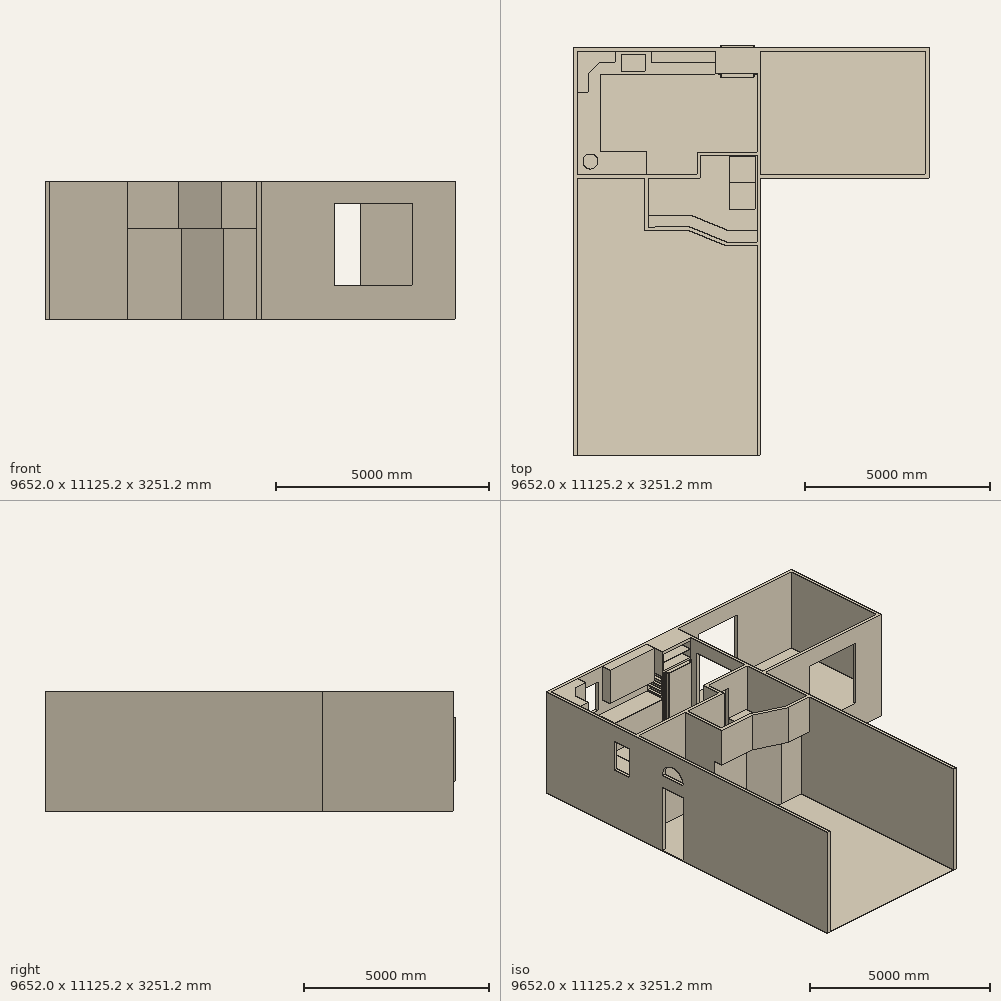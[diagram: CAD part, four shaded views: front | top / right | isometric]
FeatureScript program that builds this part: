
annotation { "Feature Type Name" : "Feature", "Feature Type Description" : "" }
export const myFeature = defineFeature(function(context is Context, id is Id, definition is map)
    precondition{}
    {
        {
            var Q0;
            Q0=qCreatedBy(makeId("Top.planeOp"),FACE);
            var sketch = newSketch(context, id + "F0", { "sketchPlane" : qUnion([Q0])});
            skLineSegment(sketch, "E0.bottom", {"start": v(-4876.8, 3352.8) * mm, "end": v(4572, 3352.8) * mm});
            skLineSegment(sketch, "E0.top", {"start": v(0, 0) * mm, "end": v(4572, 0) * mm});
            skLineSegment(sketch, "E0.left", {"start": v(-4876.8, 3352.8) * mm, "end": v(-4876.8, 0) * mm});
            skLineSegment(sketch, "E0.right", {"start": v(4572, 3352.8) * mm, "end": v(4572, 0) * mm});
            skLineSegment(sketch, "E1.left", {"start": v(-4876.8, 0) * mm, "end": v(-4876.8, -7620) * mm});
            skLineSegment(sketch, "E1.right", {"start": v(0, 0) * mm, "end": v(0, -7620) * mm});
            skLineSegment(sketch, "E2.0", {"start": v(101.6, -101.6) * mm, "end": v(101.6, -7620) * mm});
            skLineSegment(sketch, "E2.1", {"start": v(101.6, -101.6) * mm, "end": v(4673.6, -101.6) * mm});
            skLineSegment(sketch, "E2.2", {"start": v(-4978.4, 0) * mm, "end": v(-4978.4, -7620) * mm});
            skLineSegment(sketch, "E2.3", {"start": v(-4978.4, 3454.4) * mm, "end": v(-4978.4, 0) * mm});
            skLineSegment(sketch, "E2.4", {"start": v(-4978.4, 3454.4) * mm, "end": v(4673.6, 3454.4) * mm});
            skLineSegment(sketch, "E2.5", {"start": v(4673.6, 3454.4) * mm, "end": v(4673.6, -101.6) * mm});
            skLineSegment(sketch, "E3", {"start": v(-4978.4, -7620) * mm, "end": v(-4876.8, -7620) * mm});
            skLineSegment(sketch, "E4", {"start": v(0, -7620) * mm, "end": v(101.6, -7620) * mm});
            skSolve(sketch);
        }
        {
            var Q0;
            Q0=qSketchRegion(id+"F0",true);
            extrude(context, id + "F1", {"entities" : qUnion([Q0]), "depth" : 3251.2 * mm});
        }
        {
            var Q0;
            Q0=qCreatedBy(makeId("Top.planeOp"),FACE);
            var sketch = newSketch(context, id + "F2", { "sketchPlane" : qUnion([Q0])});
            skLineSegment(sketch, "E5.0", {"start": v(-4876.8, 3352.8) * mm, "end": v(-4876.8, -7620) * mm});
            skLineSegment(sketch, "E6.0", {"start": v(-4876.8, 3352.8) * mm, "end": v(4572, 3352.8) * mm});
            skLineSegment(sketch, "E7.0", {"start": v(4572, 3352.8) * mm, "end": v(4572, 0) * mm});
            skLineSegment(sketch, "E8.0", {"start": v(0, 0) * mm, "end": v(4572, 0) * mm});
            skLineSegment(sketch, "E9.0", {"start": v(0, 0) * mm, "end": v(0, -7620) * mm});
            skLineSegment(sketch, "E10", {"start": v(-4876.8, -7620) * mm, "end": v(0, -7620) * mm});
            skSolve(sketch);
        }
        {
            var Q0;
            Q0=qSketchRegion(id+"F2",true);
            extrude(context, id + "F3", {"entities" : qUnion([Q0]), "operationType" : NewBodyOperationType.ADD, "depth" : 812.8 * mm});
        }
        {
            var Q0;
            Q0=makeQuery(id+"F3.opExtrude","CAP_FACE",FACE,{"disambiguationData":[OSD([sQuery(id+"F2.wireOp",EDGE,"E5.0"),sQuery(id+"F2.wireOp",EDGE,"E6.0"),sQuery(id+"F2.wireOp",EDGE,"E7.0"),sQuery(id+"F2.wireOp",EDGE,"E8.0"),sQuery(id+"F2.wireOp",EDGE,"E9.0"),sQuery(id+"F2.wireOp",EDGE,"E10")])],"isStart":false});
            var sketch = newSketch(context, id + "F4", { "sketchPlane" : qUnion([Q0])});
            skLineSegment(sketch, "E11", {"start": v(-4876.8, 0) * mm, "end": v(-3048, 0) * mm});
            skLineSegment(sketch, "E12", {"start": v(-3048, -1219.2) * mm, "end": v(-1778, -1219.2) * mm});
            skLineSegment(sketch, "E13", {"start": v(0, -1625.6) * mm, "end": v(0, -7620) * mm});
            skLineSegment(sketch, "E14", {"start": v(0, -7620) * mm, "end": v(-4876.8, -7620) * mm});
            skLineSegment(sketch, "E15", {"start": v(-4876.8, -7620) * mm, "end": v(-4876.8, 0) * mm});
            skLineSegment(sketch, "E16", {"start": v(-3048, 0) * mm, "end": v(-3048, -1219.2) * mm});
            skLineSegment(sketch, "E17", {"start": v(-1778, -1219.2) * mm, "end": v(-781.81, -1625.6) * mm});
            skLineSegment(sketch, "E18", {"start": v(-781.81, -1625.6) * mm, "end": v(0, -1625.6) * mm});
            skSolve(sketch);
        }
        {
            var Q0;
            Q0=qSketchRegion(id+"F4",true);
            extrude(context, id + "F5", {"entities" : qUnion([Q0]), "operationType" : NewBodyOperationType.REMOVE, "oppositeDirection" : true, "depth" : 800.1 * mm});
        }
        {
            var Q0;
            Q0=makeQuery(id+"F1.opExtrude","CAP_FACE",FACE,{"disambiguationData":[OSD([sQuery(id+"F0.wireOp",EDGE,"E0.bottom"),sQuery(id+"F0.wireOp",EDGE,"E0.top"),sQuery(id+"F0.wireOp",EDGE,"E0.left"),sQuery(id+"F0.wireOp",EDGE,"E0.right"),sQuery(id+"F0.wireOp",EDGE,"E1.left"),sQuery(id+"F0.wireOp",EDGE,"E1.right"),sQuery(id+"F0.wireOp",EDGE,"E2.0"),sQuery(id+"F0.wireOp",EDGE,"E2.1"),sQuery(id+"F0.wireOp",EDGE,"E2.2"),sQuery(id+"F0.wireOp",EDGE,"E2.3"),sQuery(id+"F0.wireOp",EDGE,"E2.4"),sQuery(id+"F0.wireOp",EDGE,"E2.5"),sQuery(id+"F0.wireOp",EDGE,"E3"),sQuery(id+"F0.wireOp",EDGE,"E4")])],"isStart":false});
            var sketch = newSketch(context, id + "F6", { "sketchPlane" : qUnion([Q0])});
            skLineSegment(sketch, "E19", {"start": v(-1625.6, 0) * mm, "end": v(-4876.8, 0) * mm});
            skLineSegment(sketch, "E20", {"start": v(-4876.8, 0) * mm, "end": v(-4876.8, -101.6) * mm});
            skLineSegment(sketch, "E21", {"start": v(-4876.8, -101.6) * mm, "end": v(-3048, -101.6) * mm});
            skLineSegment(sketch, "E22", {"start": v(-781.93, -1625.6) * mm, "end": v(-1778, -1219.2) * mm});
            skLineSegment(sketch, "E23", {"start": v(-1758.07, -1117.6) * mm, "end": v(-762, -1524) * mm});
            skLineSegment(sketch, "E24", {"start": v(-1778, -1219.2) * mm, "end": v(-3048, -1219.2) * mm});
            skLineSegment(sketch, "E25", {"start": v(-2946.4, -1117.6) * mm, "end": v(-1758.07, -1117.6) * mm});
            skPoint(sketch, "E26.orphan", {"position": v(-1778, -1117.6) * mm});
            skLineSegment(sketch, "E27", {"start": v(-3048, -1219.2) * mm, "end": v(-3048, -101.6) * mm});
            skLineSegment(sketch, "E28", {"start": v(-2946.4, -1117.6) * mm, "end": v(-2946.4, -101.6) * mm});
            skLineSegment(sketch, "E29.trimOffspring", {"start": v(-2946.4, -101.6) * mm, "end": v(-1524, -101.6) * mm});
            skLineSegment(sketch, "E30", {"start": v(-762, -1524) * mm, "end": v(0, -1524) * mm});
            skLineSegment(sketch, "E31", {"start": v(0, -1524) * mm, "end": v(0, -1625.6) * mm});
            skLineSegment(sketch, "E32", {"start": v(0, -1625.6) * mm, "end": v(-781.93, -1625.6) * mm});
            skLineSegment(sketch, "E33", {"start": v(0, 508) * mm, "end": v(-1524, 508) * mm});
            skLineSegment(sketch, "E34", {"start": v(-1524, 508) * mm, "end": v(-1524, -101.6) * mm});
            skLineSegment(sketch, "E35", {"start": v(0, 609.6) * mm, "end": v(-1625.6, 609.6) * mm});
            skLineSegment(sketch, "E36", {"start": v(-1625.6, 609.6) * mm, "end": v(-1625.6, 0) * mm});
            skLineSegment(sketch, "E37", {"start": v(0, 609.6) * mm, "end": v(0, 508) * mm});
            skSolve(sketch);
        }
        {
            var Q0;
            Q0=qSketchRegion(id+"F6",true);
            extrude(context, id + "F7", {"entities" : qUnion([Q0]), "endBound" : BoundingType.UP_TO_NEXT, "oppositeDirection" : true, "depth" : 25.4 * mm});
        }
        {
            var Q0;
            Q0=makeQuery(id+"F1.opExtrude","SWEPT_FACE",FACE,{"disambiguationData":[OSD([sQuery(id+"F0.wireOp",EDGE,"E2.2"),sQuery(id+"F0.wireOp",EDGE,"E2.3")])]});
            var sketch = newSketch(context, id + "F8", { "sketchPlane" : qUnion([Q0])});
            skLineSegment(sketch, "E38.bottom", {"start": v(1930.4, 12.7) * mm, "end": v(1117.6, 12.7) * mm});
            skLineSegment(sketch, "E38.top", {"start": v(1930.4, 2044.7) * mm, "end": v(1117.6, 2044.7) * mm});
            skLineSegment(sketch, "E38.left", {"start": v(1930.4, 12.7) * mm, "end": v(1930.4, 2044.7) * mm});
            skLineSegment(sketch, "E38.right", {"start": v(1117.6, 12.7) * mm, "end": v(1117.6, 2044.7) * mm});
            skLineSegment(sketch, "E39", {"start": v(1117.6, 2425.7) * mm, "end": v(1930.4, 2425.7) * mm});
            skArc(sketch, "E40", {"start": v(1930.4, 2425.7) * mm, "mid": v(1524, 2832.1) * mm, "end": v(1117.6, 2425.7) * mm});
            skSolve(sketch);
        }
        {
            var Q0;
            Q0=qSketchRegion(id+"F8",true);
            extrude(context, id + "F9", {"entities" : qUnion([Q0]), "operationType" : NewBodyOperationType.REMOVE, "oppositeDirection" : true, "depth" : 101.6 * mm});
        }
        {
            var Q0;
            Q0=makeQuery(id+"F1.opExtrude","SWEPT_FACE",FACE,{"disambiguationData":[OSD([sQuery(id+"F0.wireOp",EDGE,"E2.2"),sQuery(id+"F0.wireOp",EDGE,"E2.3")])]});
            var sketch = newSketch(context, id + "F10", { "sketchPlane" : qUnion([Q0])});
            skLineSegment(sketch, "E41.bottom", {"start": v(-787.4, 2743.2) * mm, "end": v(-177.8, 2743.2) * mm});
            skLineSegment(sketch, "E41.top", {"start": v(-787.4, 1828.8) * mm, "end": v(-177.8, 1828.8) * mm});
            skLineSegment(sketch, "E41.left", {"start": v(-787.4, 2743.2) * mm, "end": v(-787.4, 1828.8) * mm});
            skLineSegment(sketch, "E41.right", {"start": v(-177.8, 2743.2) * mm, "end": v(-177.8, 1828.8) * mm});
            skSolve(sketch);
        }
        {
            var Q0;
            Q0=qSketchRegion(id+"F10",true);
            extrude(context, id + "F11", {"entities" : qUnion([Q0]), "operationType" : NewBodyOperationType.REMOVE, "oppositeDirection" : true, "depth" : 101.6 * mm});
        }
        {
            var Q0;
            Q0=makeQuery(id+"FPiMINyQIs0wdXI_2.boolean.opBoolean","SPLIT",FACE,{"disambiguationData":[TD([makeQuery(id+"F1.opExtrude","SWEPT_FACE",FACE,{"disambiguationData":[OSD([sQuery(id+"F0.wireOp",EDGE,"E0.bottom")])]})])],"derivedFrom":makeQuery(id+"F3.opExtrude","CAP_FACE",FACE,{"disambiguationData":[OSD([sQuery(id+"F2.wireOp",EDGE,"E5.0"),sQuery(id+"F2.wireOp",EDGE,"E6.0"),sQuery(id+"F2.wireOp",EDGE,"E7.0"),sQuery(id+"F2.wireOp",EDGE,"E8.0"),sQuery(id+"F2.wireOp",EDGE,"E9.0"),sQuery(id+"F2.wireOp",EDGE,"E10")])],"isStart":false})});
            var sketch = newSketch(context, id + "F12", { "sketchPlane" : qUnion([Q0])});
            skLineSegment(sketch, "E42.top", {"start": v(-4876.8, 3352.8) * mm, "end": v(-4292.6, 3352.8) * mm});
            skLineSegment(sketch, "E42.left", {"start": v(-4876.8, 0) * mm, "end": v(-4876.8, 3352.8) * mm});
            skLineSegment(sketch, "E43.bottom", {"start": v(-4292.6, 3352.8) * mm, "end": v(-1117.6, 3352.8) * mm});
            skLineSegment(sketch, "E43.top", {"start": v(-4267.2, 2743.2) * mm, "end": v(-1117.6, 2743.2) * mm});
            skLineSegment(sketch, "E43.right", {"start": v(-1117.6, 3352.8) * mm, "end": v(-1117.6, 2743.2) * mm});
            skLineSegment(sketch, "E44", {"start": v(-4267.2, 2743.2) * mm, "end": v(-4267.2, 609.6) * mm});
            skLineSegment(sketch, "E45", {"start": v(-4267.2, 609.6) * mm, "end": v(-2997.2, 609.6) * mm});
            skLineSegment(sketch, "E46", {"start": v(-2997.2, 609.6) * mm, "end": v(-2997.2, 0) * mm});
            skLineSegment(sketch, "E47", {"start": v(-2997.2, 0) * mm, "end": v(-4876.8, 0) * mm});
            skSolve(sketch);
        }
        {
            var Q0;
            Q0=qSketchRegion(id+"F12",true);
            extrude(context, id + "F13", {"entities" : qUnion([Q0]), "depth" : 914.4 * mm});
        }
        {
            var Q0;
            Q0=makeQuery(id+"F13.opExtrude","CAP_FACE",FACE,{"disambiguationData":[OSD([sQuery(id+"F12.wireOp",EDGE,"E42.bottom"),sQuery(id+"F12.wireOp",EDGE,"E42.top"),sQuery(id+"F12.wireOp",EDGE,"E42.left"),sQuery(id+"F12.wireOp",EDGE,"E42.right"),sQuery(id+"F12.wireOp",EDGE,"E43.bottom"),sQuery(id+"F12.wireOp",EDGE,"E43.top"),sQuery(id+"F12.wireOp",EDGE,"E43.right")])],"isStart":false});
            var sketch = newSketch(context, id + "F14", { "sketchPlane" : qUnion([Q0])});
            skLineSegment(sketch, "E48", {"start": v(-1117.6, 3352.8) * mm, "end": v(-1117.6, 2717.8) * mm});
            skLineSegment(sketch, "E49", {"start": v(-1117.6, 2717.8) * mm, "end": v(-4241.8, 2717.8) * mm});
            skLineSegment(sketch, "E50", {"start": v(-4241.8, 2717.8) * mm, "end": v(-4241.8, 635) * mm});
            skLineSegment(sketch, "E51", {"start": v(-4241.8, 635) * mm, "end": v(-2997.2, 635) * mm});
            skLineSegment(sketch, "E52", {"start": v(-2997.2, 635) * mm, "end": v(-2997.2, 0) * mm});
            skLineSegment(sketch, "E53", {"start": v(-2997.2, 0) * mm, "end": v(-4876.8, 0) * mm});
            skLineSegment(sketch, "E54", {"start": v(-4876.8, 0) * mm, "end": v(-4876.8, 3352.8) * mm});
            skLineSegment(sketch, "E55", {"start": v(-4876.8, 3352.8) * mm, "end": v(-1117.6, 3352.8) * mm});
            skSolve(sketch);
        }
        {
            var Q0;
            Q0=qSketchRegion(id+"F14",true);
            extrude(context, id + "F15", {"entities" : qUnion([Q0]), "depth" : 19.05 * mm});
        }
        {
            var Q0;
            Q0=makeQuery(id+"F1.opExtrude","SWEPT_FACE",FACE,{"disambiguationData":[OSD([sQuery(id+"F0.wireOp",EDGE,"E2.1")])]});
            var sketch = newSketch(context, id + "F16", { "sketchPlane" : qUnion([Q0])});
            skLineSegment(sketch, "E56.bottom", {"start": v(1828.8, 2743.2) * mm, "end": v(3657.6, 2743.2) * mm});
            skLineSegment(sketch, "E56.top", {"start": v(1828.8, 812.8) * mm, "end": v(3657.6, 812.8) * mm});
            skLineSegment(sketch, "E56.left", {"start": v(1828.8, 2743.2) * mm, "end": v(1828.8, 812.8) * mm});
            skLineSegment(sketch, "E56.right", {"start": v(3657.6, 2743.2) * mm, "end": v(3657.6, 812.8) * mm});
            skSolve(sketch);
        }
        {
            var Q0;
            Q0=qSketchRegion(id+"F16",true);
            extrude(context, id + "F17", {"entities" : qUnion([Q0]), "operationType" : NewBodyOperationType.REMOVE, "oppositeDirection" : true, "depth" : 101.6 * mm});
        }
        {
            var Q0;
            Q0=makeQuery(id+"F1.opExtrude","SWEPT_FACE",FACE,{"disambiguationData":[OSD([sQuery(id+"F0.wireOp",EDGE,"E2.4")])]});
            var sketch = newSketch(context, id + "F18", { "sketchPlane" : qUnion([Q0])});
            skLineSegment(sketch, "E57.bottom", {"start": v(-2438.4, 2743.2) * mm, "end": v(-914.4, 2743.2) * mm});
            skLineSegment(sketch, "E57.top", {"start": v(-2438.4, 812.8) * mm, "end": v(-914.4, 812.8) * mm});
            skLineSegment(sketch, "E57.left", {"start": v(-2438.4, 2743.2) * mm, "end": v(-2438.4, 812.8) * mm});
            skLineSegment(sketch, "E57.right", {"start": v(-914.4, 2743.2) * mm, "end": v(-914.4, 812.8) * mm});
            skLineSegment(sketch, "E58.bottom", {"start": v(3048, 2813.05) * mm, "end": v(3657.6, 2813.05) * mm});
            skLineSegment(sketch, "E58.top", {"start": v(3048, 1898.65) * mm, "end": v(3657.6, 1898.65) * mm});
            skLineSegment(sketch, "E58.left", {"start": v(3048, 2813.05) * mm, "end": v(3048, 1898.65) * mm});
            skLineSegment(sketch, "E58.right", {"start": v(3657.6, 2813.05) * mm, "end": v(3657.6, 1898.65) * mm});
            skSolve(sketch);
        }
        {
            var Q0;
            Q0=qSketchRegion(id+"F18",true);
            extrude(context, id + "F19", {"entities" : qUnion([Q0]), "operationType" : NewBodyOperationType.REMOVE, "oppositeDirection" : true, "depth" : 101.6 * mm});
        }
        {
            var Q0;
            Q0=makeQuery(id+"F19.boolean.opBoolean","MERGE",FACE,{"derivedFrom":[makeQuery(id+"F17.boolean.opBoolean","MERGE",FACE,{"derivedFrom":[makeQuery(id+"FPiMINyQIs0wdXI_2.boolean.opBoolean","SPLIT",FACE,{"disambiguationData":[TD([makeQuery(id+"F1.opExtrude","SWEPT_FACE",FACE,{"disambiguationData":[OSD([sQuery(id+"F0.wireOp",EDGE,"E0.bottom")])]})])],"derivedFrom":makeQuery(id+"F3.opExtrude","CAP_FACE",FACE,{"disambiguationData":[OSD([sQuery(id+"F2.wireOp",EDGE,"E5.0"),sQuery(id+"F2.wireOp",EDGE,"E6.0"),sQuery(id+"F2.wireOp",EDGE,"E7.0"),sQuery(id+"F2.wireOp",EDGE,"E8.0"),sQuery(id+"F2.wireOp",EDGE,"E9.0"),sQuery(id+"F2.wireOp",EDGE,"E10")])],"isStart":false})}),makeQuery(id+"F17.opExtrude","SWEPT_FACE",FACE,{"disambiguationData":[OSD([sQuery(id+"F16.wireOp",EDGE,"E56.top")])]})]}),makeQuery(id+"F19.opExtrude","SWEPT_FACE",FACE,{"disambiguationData":[OSD([sQuery(id+"F18.wireOp",EDGE,"E57.top")])]})]});
            var sketch = newSketch(context, id + "F20", { "sketchPlane" : qUnion([Q0])});
            skLineSegment(sketch, "E59.bottom", {"start": v(-984.25, 3505.2) * mm, "end": v(-76.2, 3505.2) * mm});
            skLineSegment(sketch, "E59.top", {"start": v(-984.25, 2625.73) * mm, "end": v(-76.2, 2625.73) * mm});
            skLineSegment(sketch, "E59.left", {"start": v(-984.25, 3505.2) * mm, "end": v(-984.25, 2625.73) * mm});
            skLineSegment(sketch, "E59.right", {"start": v(-76.2, 3505.2) * mm, "end": v(-76.2, 2625.73) * mm});
            skSolve(sketch);
        }
        {
            var Q0;
            Q0=makeQuery(id+"F15.opExtrude","CAP_FACE",FACE,{"disambiguationData":[OSD([sQuery(id+"F14.wireOp",EDGE,"E48"),sQuery(id+"F14.wireOp",EDGE,"E49"),sQuery(id+"F14.wireOp",EDGE,"E50"),sQuery(id+"F14.wireOp",EDGE,"E51"),sQuery(id+"F14.wireOp",EDGE,"E52"),sQuery(id+"F14.wireOp",EDGE,"E53"),sQuery(id+"F14.wireOp",EDGE,"E54"),sQuery(id+"F14.wireOp",EDGE,"E55")])],"isStart":false});
            var sketch = newSketch(context, id + "F21", { "sketchPlane" : qUnion([Q0])});
            skLineSegment(sketch, "E60.bottom", {"start": v(-3670.3, 3251.2) * mm, "end": v(-3035.3, 3251.2) * mm});
            skLineSegment(sketch, "E60.top", {"start": v(-3670.3, 2794) * mm, "end": v(-3035.3, 2794) * mm});
            skLineSegment(sketch, "E60.left", {"start": v(-3683, 3238.5) * mm, "end": v(-3683, 2806.7) * mm});
            skLineSegment(sketch, "E60.right", {"start": v(-3022.6, 3238.5) * mm, "end": v(-3022.6, 2806.7) * mm});
            skPoint(sketch, "E61.visualSharp", {"position": v(-3683, 3251.2) * mm});
            skArc(sketch, "E61.filletArc", {"start": v(-3670.3, 3251.2) * mm, "mid": v(-3679.28, 3247.48) * mm, "end": v(-3683, 3238.5) * mm});
            skPoint(sketch, "E62.visualSharp", {"position": v(-3683, 2794) * mm});
            skArc(sketch, "E62.filletArc", {"start": v(-3683, 2806.7) * mm, "mid": v(-3679.28, 2797.72) * mm, "end": v(-3670.3, 2794) * mm});
            skPoint(sketch, "E63.visualSharp", {"position": v(-3022.6, 2794) * mm});
            skArc(sketch, "E63.filletArc", {"start": v(-3035.3, 2794) * mm, "mid": v(-3026.32, 2797.72) * mm, "end": v(-3022.6, 2806.7) * mm});
            skPoint(sketch, "E64.visualSharp", {"position": v(-3022.6, 3251.2) * mm});
            skArc(sketch, "E64.filletArc", {"start": v(-3022.6, 3238.5) * mm, "mid": v(-3026.32, 3247.48) * mm, "end": v(-3035.3, 3251.2) * mm});
            skCircle(sketch, "E65", {"center": v(-4521.2, 355.6) * mm, "radius": 203.2 * mm});
            skSolve(sketch);
        }
        {
            var Q0;
            Q0=qSketchRegion(id+"F21",true);
            extrude(context, id + "F22", {"entities" : qUnion([Q0]), "operationType" : NewBodyOperationType.REMOVE, "oppositeDirection" : true, "depth" : 304.8 * mm});
        }
        {
            var Q0;
            Q0=makeQuery(id+"FH5c1B8FBqfH3I5_2.boolean.opBoolean","MERGE",FACE,{"derivedFrom":[makeQuery(id+"FPiMINyQIs0wdXI_2.boolean.opBoolean","MERGE",FACE,{"derivedFrom":[makeQuery(id+"F1.opExtrude","CAP_FACE",FACE,{"disambiguationData":[OSD([sQuery(id+"F0.wireOp",EDGE,"E0.bottom"),sQuery(id+"F0.wireOp",EDGE,"E0.top"),sQuery(id+"F0.wireOp",EDGE,"E0.left"),sQuery(id+"F0.wireOp",EDGE,"E0.right"),sQuery(id+"F0.wireOp",EDGE,"E1.left"),sQuery(id+"F0.wireOp",EDGE,"E1.right"),sQuery(id+"F0.wireOp",EDGE,"E2.0"),sQuery(id+"F0.wireOp",EDGE,"E2.1"),sQuery(id+"F0.wireOp",EDGE,"E2.2"),sQuery(id+"F0.wireOp",EDGE,"E2.3"),sQuery(id+"F0.wireOp",EDGE,"E2.4"),sQuery(id+"F0.wireOp",EDGE,"E2.5"),sQuery(id+"F0.wireOp",EDGE,"E3"),sQuery(id+"F0.wireOp",EDGE,"E4")])],"isStart":false}),makeQuery(id+"FPiMINyQIs0wdXI_2.opExtrude","CAP_FACE",FACE,{"disambiguationData":[OSD([sQuery(id+"FEc21F3D3GuDDtd_2.wireOp",EDGE,"934bb5f1-d7c1-477a-a7d4-6400566a4c75.bottom"),sQuery(id+"FEc21F3D3GuDDtd_2.wireOp",EDGE,"934bb5f1-d7c1-477a-a7d4-6400566a4c75.top"),sQuery(id+"FEc21F3D3GuDDtd_2.wireOp",EDGE,"934bb5f1-d7c1-477a-a7d4-6400566a4c75.right"),sQuery(id+"FEc21F3D3GuDDtd_2.wireOp",EDGE,"e5cfa449-8771-4456-8ad2-e5eecc279019.bottom"),sQuery(id+"FEc21F3D3GuDDtd_2.wireOp",EDGE,"e5cfa449-8771-4456-8ad2-e5eecc279019.top"),sQuery(id+"FEc21F3D3GuDDtd_2.wireOp",EDGE,"e5cfa449-8771-4456-8ad2-e5eecc279019.right"),sQuery(id+"FEc21F3D3GuDDtd_2.wireOp",EDGE,"OCDYTF2m-4J0G-WOIT-R1Ji-ORLyYsqLIilW"),sQuery(id+"FEc21F3D3GuDDtd_2.wireOp",EDGE,"0kAvmwYa-p2tX-TsP0-lfS8-sPPEvB1fLYrj")])],"isStart":false})]}),makeQuery(id+"FH5c1B8FBqfH3I5_2.opExtrude","CAP_FACE",FACE,{"disambiguationData":[OSD([sQuery(id+"FxzC0NgOfVmASQ0_2.wireOp",EDGE,"857f3de3-4ae1-46da-a041-e3c2da7e36f9.bottom"),sQuery(id+"FxzC0NgOfVmASQ0_2.wireOp",EDGE,"857f3de3-4ae1-46da-a041-e3c2da7e36f9.top"),sQuery(id+"FxzC0NgOfVmASQ0_2.wireOp",EDGE,"857f3de3-4ae1-46da-a041-e3c2da7e36f9.left"),sQuery(id+"FxzC0NgOfVmASQ0_2.wireOp",EDGE,"857f3de3-4ae1-46da-a041-e3c2da7e36f9.right")])],"isStart":false})]});
            var sketch = newSketch(context, id + "F23", { "sketchPlane" : qUnion([Q0])});
            skLineSegment(sketch, "E66.top", {"start": v(-4876.8, 2216.71) * mm, "end": v(-4572, 2216.71) * mm});
            skLineSegment(sketch, "E66.left", {"start": v(-4876.8, 3352.8) * mm, "end": v(-4876.8, 2216.71) * mm});
            skLineSegment(sketch, "E67.top", {"start": v(-4248.71, 3048) * mm, "end": v(-3842.31, 3048) * mm});
            skLineSegment(sketch, "E67.right", {"start": v(-3842.31, 3352.8) * mm, "end": v(-3842.31, 3048) * mm});
            skLineSegment(sketch, "E68", {"start": v(-4572, 2724.71) * mm, "end": v(-4248.71, 3048) * mm});
            skLineSegment(sketch, "E69.trimOffspring", {"start": v(-4572, 2724.71) * mm, "end": v(-4572, 2216.71) * mm});
            skLineSegment(sketch, "E70", {"start": v(-4876.8, 3352.8) * mm, "end": v(-3842.31, 3352.8) * mm});
            skLineSegment(sketch, "E71.bottom", {"start": v(-2877.11, 3352.8) * mm, "end": v(-1117.6, 3352.8) * mm});
            skLineSegment(sketch, "E71.top", {"start": v(-2877.11, 3048) * mm, "end": v(-1117.6, 3048) * mm});
            skLineSegment(sketch, "E71.left", {"start": v(-2877.11, 3352.8) * mm, "end": v(-2877.11, 3048) * mm});
            skLineSegment(sketch, "E71.right", {"start": v(-1117.6, 3352.8) * mm, "end": v(-1117.6, 3048) * mm});
            skSolve(sketch);
        }
        {
            var Q0;
            Q0=qSketchRegion(id+"F23",true);
            extrude(context, id + "F24", {"entities" : qUnion([Q0]), "oppositeDirection" : true, "depth" : 1066.8 * mm});
        }
        {
            var Q0;
            Q0=makeQuery(id+"F1.opExtrude","SWEPT_FACE",FACE,{"disambiguationData":[OSD([sQuery(id+"F0.wireOp",EDGE,"E2.4")])]});
            var sketch = newSketch(context, id + "F25", { "sketchPlane" : qUnion([Q0])});
            skLineSegment(sketch, "E72.bottom", {"start": v(25.4, 2590.8) * mm, "end": v(990.6, 2590.8) * mm});
            skLineSegment(sketch, "E72.top", {"start": v(25.4, 812.8) * mm, "end": v(990.6, 812.8) * mm});
            skLineSegment(sketch, "E72.left", {"start": v(25.4, 2590.8) * mm, "end": v(25.4, 812.8) * mm});
            skLineSegment(sketch, "E72.right", {"start": v(990.6, 2590.8) * mm, "end": v(990.6, 812.8) * mm});
            skSolve(sketch);
        }
        {
            var Q0;
            Q0 = qSketchRegion(id + "F25", true);
            extrude(context, id + "F26", {"entities" : qUnion([Q0]), "operationType" : NewBodyOperationType.REMOVE, "oppositeDirection" : true, "depth" : 101.6 * mm});
        }
        {
            var Q0;
            Q0=qSketchRegion(id+"F20",true);
            extrude(context, id + "F27", {"entities" : qUnion([Q0]), "depth" : 1739.9 * mm});
        }
        {
            var Q0;
            Q0=makeQuery(id+"F1.opExtrude","SWEPT_FACE",FACE,{"disambiguationData":[OSD([sQuery(id+"F0.wireOp",EDGE,"E0.bottom")])]});
            var sketch = newSketch(context, id + "F28", { "sketchPlane" : qUnion([Q0])});
            skLineSegment(sketch, "E73", {"start": v(-1117.6, 812.8) * mm, "end": v(-1117.6, 3251.2) * mm});
            skLineSegment(sketch, "E74", {"start": v(-1117.6, 3251.2) * mm, "end": v(0, 3251.2) * mm});
            skLineSegment(sketch, "E75", {"start": v(0, 3251.2) * mm, "end": v(0, 812.8) * mm});
            skLineSegment(sketch, "E76", {"start": v(0, 812.8) * mm, "end": v(-76.2, 812.8) * mm});
            skLineSegment(sketch, "E77", {"start": v(-76.2, 812.8) * mm, "end": v(-76.2, 2552.7) * mm});
            skLineSegment(sketch, "E78", {"start": v(-76.2, 2552.7) * mm, "end": v(-984.25, 2552.7) * mm});
            skLineSegment(sketch, "E79", {"start": v(-984.25, 2552.7) * mm, "end": v(-984.25, 812.8) * mm});
            skLineSegment(sketch, "E80", {"start": v(-984.25, 812.8) * mm, "end": v(-1117.6, 812.8) * mm});
            skSolve(sketch);
        }
        {
            var Q0;
            Q0 = qSketchRegion(id + "F28", true);
            extrude(context, id + "F29", {"entities" : qUnion([Q0]), "depth" : 609.6 * mm});
        }
        {
            var Q0;
            Q0=makeQuery(id+"F27.opExtrude","SWEPT_EDGE",EDGE,{"disambiguationData":[OSD([sQuery(id+"F20.wireOp",EDGE,"E59.top"),sQuery(id+"F20.wireOp",EDGE,"E59.left")])]});
            var Q1;
            Q1=makeQuery(id+"F27.opExtrude","CAP_EDGE",EDGE,{"disambiguationData":[OSD([sQuery(id+"F20.wireOp",EDGE,"E59.left")])],"isStart":false});
            var Q2;
            Q2=makeQuery(id+"F27.opExtrude","CAP_EDGE",EDGE,{"disambiguationData":[OSD([sQuery(id+"F20.wireOp",EDGE,"E59.top")])],"isStart":false});
            var Q3;
            Q3=makeQuery(id+"F27.opExtrude","CAP_EDGE",EDGE,{"disambiguationData":[OSD([sQuery(id+"F20.wireOp",EDGE,"E59.right")])],"isStart":false});
            var Q4;
            Q4=makeQuery(id+"F27.opExtrude","SWEPT_EDGE",EDGE,{"disambiguationData":[OSD([sQuery(id+"F20.wireOp",EDGE,"E59.top"),sQuery(id+"F20.wireOp",EDGE,"E59.right")])]});
            fillet(context, id + "F30", {"entities" : qUnion([Q0, Q1, Q2, Q3, Q4]), "radius" : 12.7 * mm, "tangentPropagation" : true, "allowEdgeOverflow" : false});
        }
        {
            var Q0;
            Q0=makeQuery(id+"F26.boolean.opBoolean","MERGE",FACE,{"derivedFrom":[makeQuery(id+"F19.boolean.opBoolean","MERGE",FACE,{"derivedFrom":[makeQuery(id+"F17.boolean.opBoolean","MERGE",FACE,{"derivedFrom":[makeQuery(id+"FPiMINyQIs0wdXI_2.boolean.opBoolean","SPLIT",FACE,{"disambiguationData":[TD([makeQuery(id+"F1.opExtrude","SWEPT_FACE",FACE,{"disambiguationData":[OSD([sQuery(id+"F0.wireOp",EDGE,"E0.bottom")])]})])],"derivedFrom":makeQuery(id+"F3.opExtrude","CAP_FACE",FACE,{"disambiguationData":[OSD([sQuery(id+"F2.wireOp",EDGE,"E5.0"),sQuery(id+"F2.wireOp",EDGE,"E6.0"),sQuery(id+"F2.wireOp",EDGE,"E7.0"),sQuery(id+"F2.wireOp",EDGE,"E8.0"),sQuery(id+"F2.wireOp",EDGE,"E9.0"),sQuery(id+"F2.wireOp",EDGE,"E10")])],"isStart":false})}),makeQuery(id+"F17.opExtrude","SWEPT_FACE",FACE,{"disambiguationData":[OSD([sQuery(id+"F16.wireOp",EDGE,"E56.top")])]})]}),makeQuery(id+"F19.opExtrude","SWEPT_FACE",FACE,{"disambiguationData":[OSD([sQuery(id+"F18.wireOp",EDGE,"E57.top")])]})]}),makeQuery(id+"F26.opExtrude","SWEPT_FACE",FACE,{"disambiguationData":[OSD([sQuery(id+"F25.wireOp",EDGE,"E72.top")])]})]});
            var sketch = newSketch(context, id + "F31", { "sketchPlane" : qUnion([Q0])});
            skLineSegment(sketch, "E81.bottom", {"start": v(-984.25, 2743.2) * mm, "end": v(-1060.45, 2743.2) * mm});
            skLineSegment(sketch, "E81.top", {"start": v(-984.25, 2724.15) * mm, "end": v(-989.01, 2724.15) * mm});
            skLineSegment(sketch, "E81.left", {"start": v(-984.25, 2743.2) * mm, "end": v(-984.25, 2724.15) * mm});
            skLineSegment(sketch, "E81.right", {"start": v(-1060.45, 2743.2) * mm, "end": v(-1060.45, 2724.15) * mm});
            skArc(sketch, "E82", {"start": v(-1036.64, 2724.15) * mm, "mid": v(-1046.16, 2728.45) * mm, "end": v(-1055.69, 2724.15) * mm});
            skArc(sketch, "E83", {"start": v(-1012.83, 2724.15) * mm, "mid": v(-1022.35, 2728.45) * mm, "end": v(-1031.88, 2724.15) * mm});
            skArc(sketch, "E84", {"start": v(-989.01, 2724.15) * mm, "mid": v(-998.54, 2728.45) * mm, "end": v(-1008.06, 2724.15) * mm});
            skLineSegment(sketch, "E85.trimOffspring", {"start": v(-1055.69, 2724.15) * mm, "end": v(-1060.45, 2724.15) * mm});
            skLineSegment(sketch, "E86.trimOffspring", {"start": v(-1031.88, 2724.15) * mm, "end": v(-1036.64, 2724.15) * mm});
            skLineSegment(sketch, "E87.trimOffspring", {"start": v(-1008.06, 2724.15) * mm, "end": v(-1012.83, 2724.15) * mm});
            skArc(sketch, "E88", {"start": v(-28.57, 2724.15) * mm, "mid": v(-38.1, 2728.45) * mm, "end": v(-47.62, 2724.15) * mm});
            skLineSegment(sketch, "E89.left", {"start": v(0, 2743.2) * mm, "end": v(0, 2724.15) * mm});
            skArc(sketch, "E90", {"start": v(-4.76, 2724.15) * mm, "mid": v(-14.29, 2728.45) * mm, "end": v(-23.81, 2724.15) * mm});
            skArc(sketch, "E91", {"start": v(-52.39, 2724.15) * mm, "mid": v(-61.91, 2728.45) * mm, "end": v(-71.44, 2724.15) * mm});
            skLineSegment(sketch, "E89.right", {"start": v(-76.2, 2743.2) * mm, "end": v(-76.2, 2724.15) * mm});
            skLineSegment(sketch, "E89.bottom", {"start": v(0, 2743.2) * mm, "end": v(-76.2, 2743.2) * mm});
            skLineSegment(sketch, "E92.trimOffspring", {"start": v(-47.62, 2724.15) * mm, "end": v(-52.39, 2724.15) * mm});
            skLineSegment(sketch, "E93.trimOffspring", {"start": v(-23.81, 2724.15) * mm, "end": v(-28.57, 2724.15) * mm});
            skLineSegment(sketch, "E89.top", {"start": v(0, 2724.15) * mm, "end": v(-4.76, 2724.15) * mm});
            skLineSegment(sketch, "E94.trimOffspring", {"start": v(-71.44, 2724.15) * mm, "end": v(-76.2, 2724.15) * mm});
            skSolve(sketch);
        }
        {
            var Q0;
            Q0 = qSketchRegion(id + "F31", true);
            var Q1;
            Q1=makeQuery(id+"F27.opExtrude","CAP_FACE",FACE,{"disambiguationData":[OSD([sQuery(id+"F20.wireOp",EDGE,"E59.bottom"),sQuery(id+"F20.wireOp",EDGE,"E59.top"),sQuery(id+"F20.wireOp",EDGE,"E59.left"),sQuery(id+"F20.wireOp",EDGE,"E59.right")])],"isStart":false});
            extrude(context, id + "F32", {"entities" : qUnion([Q0]), "endBound" : BoundingType.UP_TO_SURFACE, "endBoundEntityFace" : qUnion([Q1]), "depth" : 25.4 * mm});
        }
        {
            var Q0;
            Q0=makeQuery(id+"F29.opExtrude","SWEPT_FACE",FACE,{"disambiguationData":[OSD([sQuery(id+"F28.wireOp",EDGE,"E73")])]});
            var sketch = newSketch(context, id + "F33", { "sketchPlane" : qUnion([Q0])});
            skLineSegment(sketch, "E95.bottom", {"start": v(-3327.4, 1949.45) * mm, "end": v(-2768.6, 1949.45) * mm});
            skLineSegment(sketch, "E95.top", {"start": v(-3327.4, 1797.05) * mm, "end": v(-2768.6, 1797.05) * mm});
            skLineSegment(sketch, "E95.left", {"start": v(-3327.4, 1949.45) * mm, "end": v(-3327.4, 1797.05) * mm});
            skLineSegment(sketch, "E95.right", {"start": v(-2768.6, 1949.45) * mm, "end": v(-2768.6, 1797.05) * mm});
            skLineSegment(sketch, "E96.bottom", {"start": v(-3327.4, 2114.55) * mm, "end": v(-2768.6, 2114.55) * mm});
            skLineSegment(sketch, "E96.top", {"start": v(-3327.4, 1962.15) * mm, "end": v(-2768.6, 1962.15) * mm});
            skLineSegment(sketch, "E96.left", {"start": v(-3327.4, 2114.55) * mm, "end": v(-3327.4, 1962.15) * mm});
            skLineSegment(sketch, "E96.right", {"start": v(-2768.6, 2114.55) * mm, "end": v(-2768.6, 1962.15) * mm});
            skLineSegment(sketch, "E97.bottom", {"start": v(-3327.4, 2279.65) * mm, "end": v(-2768.6, 2279.65) * mm});
            skLineSegment(sketch, "E97.top", {"start": v(-3327.4, 2127.25) * mm, "end": v(-2768.6, 2127.25) * mm});
            skLineSegment(sketch, "E97.left", {"start": v(-3327.4, 2279.65) * mm, "end": v(-3327.4, 2127.25) * mm});
            skLineSegment(sketch, "E97.right", {"start": v(-2768.6, 2279.65) * mm, "end": v(-2768.6, 2127.25) * mm});
            skLineSegment(sketch, "E98.bottom", {"start": v(-3327.4, 2444.75) * mm, "end": v(-2768.6, 2444.75) * mm});
            skLineSegment(sketch, "E98.top", {"start": v(-3327.4, 2292.35) * mm, "end": v(-2768.6, 2292.35) * mm});
            skLineSegment(sketch, "E98.left", {"start": v(-3327.4, 2444.75) * mm, "end": v(-3327.4, 2292.35) * mm});
            skLineSegment(sketch, "E98.right", {"start": v(-2768.6, 2444.75) * mm, "end": v(-2768.6, 2292.35) * mm});
            skSolve(sketch);
        }
        {
            var Q0;
            Q0 = qSketchRegion(id + "F33", true);
            extrude(context, id + "F34", {"entities" : qUnion([Q0]), "operationType" : NewBodyOperationType.REMOVE, "oppositeDirection" : true, "depth" : 101.6 * mm});
        }
        {
            var Q0;
            Q0=makeQuery(id+"F29.opExtrude","CAP_FACE",FACE,{"disambiguationData":[OSD([sQuery(id+"F28.wireOp",EDGE,"E73"),sQuery(id+"F28.wireOp",EDGE,"E74"),sQuery(id+"F28.wireOp",EDGE,"E75"),sQuery(id+"F28.wireOp",EDGE,"E76"),sQuery(id+"F28.wireOp",EDGE,"E77"),sQuery(id+"F28.wireOp",EDGE,"E78"),sQuery(id+"F28.wireOp",EDGE,"E79"),sQuery(id+"F28.wireOp",EDGE,"E80")])],"isStart":false});
            var sketch = newSketch(context, id + "F35", { "sketchPlane" : qUnion([Q0])});
            skLineSegment(sketch, "E99.bottom", {"start": v(-1098.55, 3155.95) * mm, "end": v(-19.05, 3155.95) * mm});
            skLineSegment(sketch, "E99.top", {"start": v(-1098.55, 2901.95) * mm, "end": v(-19.05, 2901.95) * mm});
            skLineSegment(sketch, "E99.left", {"start": v(-1098.55, 3155.95) * mm, "end": v(-1098.55, 2901.95) * mm});
            skLineSegment(sketch, "E99.right", {"start": v(-19.05, 3155.95) * mm, "end": v(-19.05, 2901.95) * mm});
            skLineSegment(sketch, "E100.bottom", {"start": v(-1098.55, 2882.9) * mm, "end": v(-19.05, 2882.9) * mm});
            skLineSegment(sketch, "E100.top", {"start": v(-1098.55, 2628.9) * mm, "end": v(-19.05, 2628.9) * mm});
            skLineSegment(sketch, "E100.left", {"start": v(-1098.55, 2882.9) * mm, "end": v(-1098.55, 2628.9) * mm});
            skLineSegment(sketch, "E100.right", {"start": v(-19.05, 2882.9) * mm, "end": v(-19.05, 2628.9) * mm});
            skSolve(sketch);
        }
        {
            var Q0;
            Q0 = qSketchRegion(id + "F35", true);
            extrude(context, id + "F36", {"entities" : qUnion([Q0]), "operationType" : NewBodyOperationType.REMOVE, "oppositeDirection" : true, "depth" : 558.8 * mm});
        }
        {
            var Q0;
            Q0=makeQuery(id+"F26.boolean.opBoolean","MERGE",FACE,{"derivedFrom":[makeQuery(id+"F19.boolean.opBoolean","MERGE",FACE,{"derivedFrom":[makeQuery(id+"F17.boolean.opBoolean","MERGE",FACE,{"derivedFrom":[makeQuery(id+"F3.opExtrude","CAP_FACE",FACE,{"disambiguationData":[OSD([sQuery(id+"F2.wireOp",EDGE,"E5.0"),sQuery(id+"F2.wireOp",EDGE,"E6.0"),sQuery(id+"F2.wireOp",EDGE,"E7.0"),sQuery(id+"F2.wireOp",EDGE,"E8.0"),sQuery(id+"F2.wireOp",EDGE,"E9.0"),sQuery(id+"F2.wireOp",EDGE,"E10")])],"isStart":false}),makeQuery(id+"F17.opExtrude","SWEPT_FACE",FACE,{"disambiguationData":[OSD([sQuery(id+"F16.wireOp",EDGE,"E56.top")])]})]}),makeQuery(id+"F19.opExtrude","SWEPT_FACE",FACE,{"disambiguationData":[OSD([sQuery(id+"F18.wireOp",EDGE,"E57.top")])]})]}),makeQuery(id+"F26.opExtrude","SWEPT_FACE",FACE,{"disambiguationData":[OSD([sQuery(id+"F25.wireOp",EDGE,"E72.top")])]})]});
            var sketch = newSketch(context, id + "F37", { "sketchPlane" : qUnion([Q0])});
            skLineSegment(sketch, "E101.bottom", {"start": v(-762, 495.3) * mm, "end": v(-50.8, 495.3) * mm});
            skLineSegment(sketch, "E101.top", {"start": v(-762, -203.2) * mm, "end": v(-50.8, -203.2) * mm});
            skLineSegment(sketch, "E101.left", {"start": v(-762, 495.3) * mm, "end": v(-762, -203.2) * mm});
            skLineSegment(sketch, "E101.right", {"start": v(-50.8, 495.3) * mm, "end": v(-50.8, -203.2) * mm});
            skLineSegment(sketch, "E102.bottom", {"start": v(-762, -215.9) * mm, "end": v(-44.45, -215.9) * mm});
            skLineSegment(sketch, "E102.top", {"start": v(-762, -952.5) * mm, "end": v(-44.45, -952.5) * mm});
            skLineSegment(sketch, "E102.left", {"start": v(-762, -215.9) * mm, "end": v(-762, -952.5) * mm});
            skLineSegment(sketch, "E102.right", {"start": v(-44.45, -215.9) * mm, "end": v(-44.45, -952.5) * mm});
            skSolve(sketch);
        }
        {
            var Q0;
            Q0=makeQuery(id+"F7.opExtrude","CAP_FACE",FACE,{"disambiguationData":[OSD([sQuery(id+"F6.wireOp",EDGE,"E19"),sQuery(id+"F6.wireOp",EDGE,"E20"),sQuery(id+"F6.wireOp",EDGE,"E21"),sQuery(id+"F6.wireOp",EDGE,"E22"),sQuery(id+"F6.wireOp",EDGE,"E23"),sQuery(id+"F6.wireOp",EDGE,"E24"),sQuery(id+"F6.wireOp",EDGE,"E25"),sQuery(id+"F6.wireOp",EDGE,"E27"),sQuery(id+"F6.wireOp",EDGE,"E28"),sQuery(id+"F6.wireOp",EDGE,"E29.trimOffspring"),sQuery(id+"F6.wireOp",EDGE,"E30"),sQuery(id+"F6.wireOp",EDGE,"E31"),sQuery(id+"F6.wireOp",EDGE,"E32"),sQuery(id+"F6.wireOp",EDGE,"E33"),sQuery(id+"F6.wireOp",EDGE,"E34"),sQuery(id+"F6.wireOp",EDGE,"E35"),sQuery(id+"F6.wireOp",EDGE,"E36"),sQuery(id+"F6.wireOp",EDGE,"E37")])],"isStart":true});
            var sketch = newSketch(context, id + "F38", { "sketchPlane" : qUnion([Q0])});
            skLineSegment(sketch, "E103", {"start": v(-3048, -1219.2) * mm, "end": v(-3048, -1524) * mm});
            skLineSegment(sketch, "E104", {"start": v(-781.93, -1625.6) * mm, "end": v(-781.93, -1625.6) * mm});
            skLineSegment(sketch, "E105", {"start": v(-781.93, -1625.6) * mm, "end": v(-1778, -1219.2) * mm});
            skLineSegment(sketch, "E106", {"start": v(-1778, -1219.2) * mm, "end": v(-3048, -1219.2) * mm});
            skLineSegment(sketch, "E107.0", {"start": v(-1837.79, -1524) * mm, "end": v(-3048, -1524) * mm});
            skLineSegment(sketch, "E108", {"start": v(-781.93, -1625.6) * mm, "end": v(0, -1625.6) * mm});
            skLineSegment(sketch, "E109", {"start": v(0, -1625.6) * mm, "end": v(0, -1930.4) * mm});
            skLineSegment(sketch, "E110", {"start": v(0, -1930.4) * mm, "end": v(-841.72, -1930.4) * mm});
            skLineSegment(sketch, "E111", {"start": v(-841.72, -1930.4) * mm, "end": v(-1837.79, -1524) * mm});
            skSolve(sketch);
        }
        {
            var Q0;
            Q0 = qSketchRegion(id + "F38", true);
            extrude(context, id + "F39", {"entities" : qUnion([Q0]), "operationType" : NewBodyOperationType.ADD, "oppositeDirection" : true, "depth" : 1117.6 * mm});
        }
        {
            var Q0;
            Q0=makeQuery(id+"F39.boolean.opBoolean","MERGE",FACE,{"derivedFrom":[makeQuery(id+"F7.opExtrude","CAP_FACE",FACE,{"disambiguationData":[OSD([sQuery(id+"F6.wireOp",EDGE,"E19"),sQuery(id+"F6.wireOp",EDGE,"E20"),sQuery(id+"F6.wireOp",EDGE,"E21"),sQuery(id+"F6.wireOp",EDGE,"E22"),sQuery(id+"F6.wireOp",EDGE,"E23"),sQuery(id+"F6.wireOp",EDGE,"E24"),sQuery(id+"F6.wireOp",EDGE,"E25"),sQuery(id+"F6.wireOp",EDGE,"E27"),sQuery(id+"F6.wireOp",EDGE,"E28"),sQuery(id+"F6.wireOp",EDGE,"E29.trimOffspring"),sQuery(id+"F6.wireOp",EDGE,"E30"),sQuery(id+"F6.wireOp",EDGE,"E31"),sQuery(id+"F6.wireOp",EDGE,"E32"),sQuery(id+"F6.wireOp",EDGE,"E33"),sQuery(id+"F6.wireOp",EDGE,"E34"),sQuery(id+"F6.wireOp",EDGE,"E35"),sQuery(id+"F6.wireOp",EDGE,"E36"),sQuery(id+"F6.wireOp",EDGE,"E37")])],"isStart":true}),makeQuery(id+"F39.opExtrude","CAP_FACE",FACE,{"disambiguationData":[OSD([sQuery(id+"F38.wireOp",EDGE,"E103"),sQuery(id+"F38.wireOp",EDGE,"E105"),sQuery(id+"F38.wireOp",EDGE,"E106"),sQuery(id+"F38.wireOp",EDGE,"E107.0"),sQuery(id+"F38.wireOp",EDGE,"E108"),sQuery(id+"F38.wireOp",EDGE,"E109"),sQuery(id+"F38.wireOp",EDGE,"E110"),sQuery(id+"F38.wireOp",EDGE,"E111")])],"isStart":true})]});
            var sketch = newSketch(context, id + "F40", { "sketchPlane" : qUnion([Q0])});
            skLineSegment(sketch, "E112", {"start": v(-762, -1524) * mm, "end": v(-1758.07, -1117.6) * mm});
            skLineSegment(sketch, "E113", {"start": v(-1758.07, -1117.6) * mm, "end": v(-1758.07, -1117.6) * mm});
            skLineSegment(sketch, "E114", {"start": v(-1758.07, -1117.6) * mm, "end": v(-2946.4, -1117.6) * mm});
            skLineSegment(sketch, "E115.0", {"start": v(-1857.2, -1406.35) * mm, "end": v(-2946.4, -1422.4) * mm});
            skLineSegment(sketch, "E116", {"start": v(-2946.4, -1422.4) * mm, "end": v(-2946.4, -1117.6) * mm});
            skLineSegment(sketch, "E117", {"start": v(-762, -1524) * mm, "end": v(0, -1524) * mm});
            skLineSegment(sketch, "E118", {"start": v(0, -1524) * mm, "end": v(0, -1524) * mm});
            skLineSegment(sketch, "E119", {"start": v(-1857.2, -1406.35) * mm, "end": v(-821.79, -1828.8) * mm});
            skLineSegment(sketch, "E120", {"start": v(-821.79, -1828.8) * mm, "end": v(0, -1828.8) * mm});
            skLineSegment(sketch, "E121", {"start": v(0, -1828.8) * mm, "end": v(0, -1524) * mm});
            skSolve(sketch);
        }
        {
            var Q0;
            Q0 = qSketchRegion(id + "F40", true);
            extrude(context, id + "F41", {"entities" : qUnion([Q0]), "operationType" : NewBodyOperationType.REMOVE, "oppositeDirection" : true, "depth" : 1054.1 * mm});
        }
        {
            var Q0;
            Q0=makeQuery(id+"F1.opExtrude","SWEPT_FACE",FACE,{"disambiguationData":[OSD([sQuery(id+"F0.wireOp",EDGE,"E0.top")])]});
            var sketch = newSketch(context, id + "F42", { "sketchPlane" : qUnion([Q0])});
            skLineSegment(sketch, "E122.bottom", {"start": v(0, 3251.2) * mm, "end": v(-101.6, 3251.2) * mm});
            skLineSegment(sketch, "E122.top", {"start": v(0, 812.8) * mm, "end": v(-101.6, 812.8) * mm});
            skLineSegment(sketch, "E122.left", {"start": v(0, 3251.2) * mm, "end": v(0, 812.8) * mm});
            skLineSegment(sketch, "E122.right", {"start": v(-101.6, 3251.2) * mm, "end": v(-101.6, 812.8) * mm});
            skSolve(sketch);
        }
        {
            var Q0;
            Q0=makeQuery(id+"F42.imprint","IMPRINT",FACE,{"disambiguationData":[TD([[makeQuery(id+"F42.imprint","IMPRINT",EDGE,{"derivedFrom":sQuery(id+"F42.wireOp",EDGE,"E122.bottom")}),1.0]])]});
            extrude(context, id + "F43", {"entities" : qUnion([Q0]), "operationType" : NewBodyOperationType.ADD, "depth" : 3352.8 * mm});
        }
        {
            var Q0;
            Q0=makeQuery(id+"F43.opExtrude","SWEPT_FACE",FACE,{"disambiguationData":[OSD([sQuery(id+"F42.wireOp",EDGE,"E122.right")])]});
            var sketch = newSketch(context, id + "F44", { "sketchPlane" : qUnion([Q0])});
            skLineSegment(sketch, "E123.bottom", {"start": v(685.8, 812.8) * mm, "end": v(2514.6, 812.8) * mm});
            skLineSegment(sketch, "E123.top", {"start": v(685.8, 2844.8) * mm, "end": v(2514.6, 2844.8) * mm});
            skLineSegment(sketch, "E123.left", {"start": v(685.8, 812.8) * mm, "end": v(685.8, 2844.8) * mm});
            skLineSegment(sketch, "E123.right", {"start": v(2514.6, 812.8) * mm, "end": v(2514.6, 2844.8) * mm});
            skSolve(sketch);
        }
        {
            var Q0;
            Q0 = qSketchRegion(id + "F44", true);
            extrude(context, id + "F45", {"entities" : qUnion([Q0]), "operationType" : NewBodyOperationType.REMOVE, "oppositeDirection" : true, "depth" : 101.6 * mm});
        }
        {
            var Q0;
            Q0 = qSketchRegion(id + "F37", true);
            extrude(context, id + "F46", {"entities" : qUnion([Q0]), "depth" : 1066.8 * mm});
        }
        {
            var Q0;
            Q0=makeQuery(id+"F7.opExtrude","SWEPT_FACE",FACE,{"disambiguationData":[OSD([sQuery(id+"F6.wireOp",EDGE,"E35")])]});
            var sketch = newSketch(context, id + "F47", { "sketchPlane" : qUnion([Q0])});
            skLineSegment(sketch, "E124.bottom", {"start": v(762, 2844.8) * mm, "end": v(1473.2, 2844.8) * mm});
            skLineSegment(sketch, "E124.top", {"start": v(762, 812.8) * mm, "end": v(1473.2, 812.8) * mm});
            skLineSegment(sketch, "E124.left", {"start": v(762, 2844.8) * mm, "end": v(762, 812.8) * mm});
            skLineSegment(sketch, "E124.right", {"start": v(1473.2, 2844.8) * mm, "end": v(1473.2, 812.8) * mm});
            skSolve(sketch);
        }
        {
            var Q0;
            Q0 = qSketchRegion(id + "F47", true);
            extrude(context, id + "F48", {"entities" : qUnion([Q0]), "operationType" : NewBodyOperationType.REMOVE, "oppositeDirection" : true, "depth" : 101.6 * mm});
        }
    });
